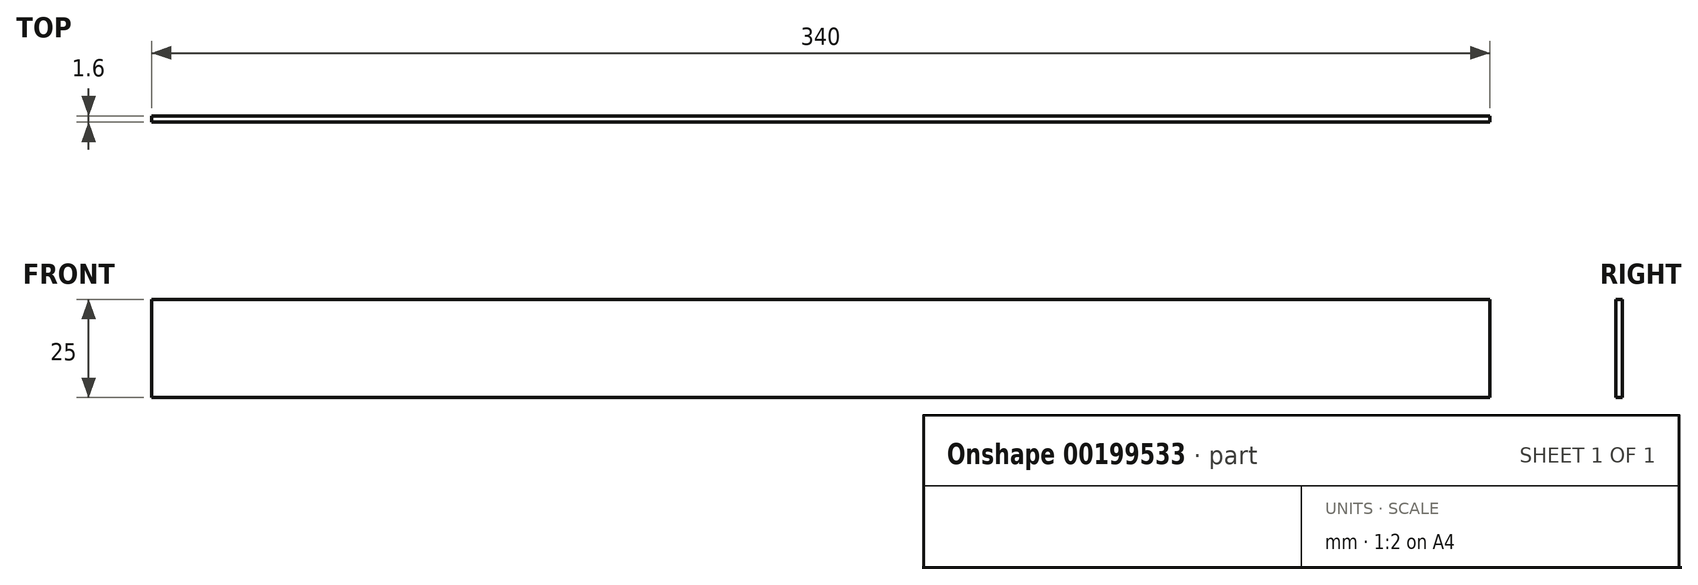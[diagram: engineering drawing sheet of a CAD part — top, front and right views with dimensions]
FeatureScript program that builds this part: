
annotation { "Feature Type Name" : "Feature", "Feature Type Description" : "" }
export const myFeature = defineFeature(function(context is Context, id is Id, definition is map)
    precondition{}
    {
        {
            var Q0;
            Q0=qCreatedBy(makeId("Front.planeOp"),FACE);
            var sketch = newSketch(context, id + "F0", { "sketchPlane" : qUnion([Q0])});
            skLineSegment(sketch, "E0.bottom", {"start": v(-165.93, -6.43) * mm, "end": v(174.07, -6.43) * mm});
            skLineSegment(sketch, "E0.top", {"start": v(-165.93, -31.43) * mm, "end": v(174.07, -31.43) * mm});
            skLineSegment(sketch, "E0.left", {"start": v(-165.93, -6.43) * mm, "end": v(-165.93, -31.43) * mm});
            skLineSegment(sketch, "E0.right", {"start": v(174.07, -6.43) * mm, "end": v(174.07, -31.43) * mm});
            skSolve(sketch);
        }
        {
            var Q0;
            Q0=makeQuery(id+"F0.imprint","IMPRINT",FACE,{"disambiguationData":[TD([[makeQuery(id+"F0.imprint","IMPRINT",EDGE,{"derivedFrom":sQuery(id+"F0.wireOp",EDGE,"E0.bottom")}),-1.0]])]});
            extrude(context, id + "F1", {"entities" : qUnion([Q0]), "depth" : 1.6 * mm});
        }
    });
